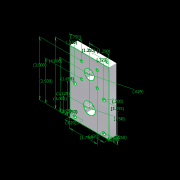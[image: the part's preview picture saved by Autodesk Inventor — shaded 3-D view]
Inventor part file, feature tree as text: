
AUTODESK INVENTOR PART (.ipt)
format: ipt  version: 2012 (Build 160160000, 160)  size: 161,792 bytes
history: native  units: in
note: dims shown in document units (in); Inventor stores cm internally (conversion verified against a paired STEP export)
features: hole x12, other x2, sketch x2, extrude x1
ambient origin geometry x8: Origin, YZ Plane, XZ Plane, XY Plane, X Axis, Y Axis, Z Axis, Center Point
bodies: Solid1 (feature_tree)
feature tree (17):
  extrude  "Extrusion1"  Depth=4.0in
  hole  "Hole15"  [1 undecoded]
  hole  "Hole16"  [1 undecoded]
  hole  "Hole17"  [1 undecoded]
  hole  "Hole18"  [1 undecoded]
  hole  "Hole19"  [1 undecoded]
  hole  "Hole20"  [1 undecoded]
  hole  "Hole23"  [1 undecoded]
  hole  "Hole24"  [1 undecoded]
  other  "Font"
  other  "Side"
  hole  "Hole25"  [1 undecoded]
  hole  "Hole26"  [1 undecoded]
  hole  "Hole27"  [1 undecoded]
  hole  "Hole28"  [1 undecoded]
  sketch  "Sketch5"  dims[d2=0.5in d3=0.0in d130=0.32in d131=0.195in d132=0.2in d133=0.75in d134=0.375in d135=0.25in d136=0.5635in d137=0.5in d138=0.8108in d139=0.32in d140=0.195in d141=0.2in d142=0.75in d143=0.375in d144=0.25in d145=0.5635in d146=0.5in d147=0.8108in d148=0.32in d149=2.055in d150=0.2in d151=0.75in d152=0.375in d153=0.25in d154=0.5635in d155=0.5in d156=0.8108in d157=0.32in d158=2.055in d159=0.2in d160=0.75in d161=0.375in d162=0.25in d163=0.5635in d164=0.5in d165=0.8108in d166=1.0in d167=1.25in d168=0.629in d169=0.75in d170=0.375in d171=0.25in d172=0.5635in d173=0.5in d174=0.8108in d175=1.25in d176=1.125in d177=0.75in d178=0.75in d179=0.375in d180=0.25in d181=0.5635in d182=0.5in d183=0.8108in d202=0.25in d203=0.62in d204=0.159in d205=0.75in d206=0.375in d207=0.25in d208=0.5635in d209=2.0in d210=0.8108in d211=0.25in d212=0.62in d213=0.159in d214=0.75in d215=0.375in d216=0.25in d217=0.5635in d218=2.0in d219=0.8108in d220=4.0in d221=0.2in d222=0.629in d223=0.75in d224=0.32in d225=0.195in d226=1.125in d227=3.0in d228=0.32in d229=0.195in d230=2.055in d231=2.055in d232=0.62in d233=0.5in d234=0.62in d235=0.25in d236=0.25in d237=1.25in d238=1.25in d239=0.75in d240=3.5in d241=0.155in d242=0.75in d243=0.375in d244=0.25in d245=0.5635in d246=1.0in d247=0.8108in d248=0.75in d249=2.5in d250=0.155in d251=0.75in d252=0.375in d253=0.25in d254=0.5635in d255=1.0in d256=0.8108in d257=1.75in d258=3.5in d259=0.155in d260=0.75in d261=0.375in d262=0.25in d263=0.5635in d264=1.0in d265=0.8108in d266=1.75in d267=2.5in d268=0.155in d269=0.75in d270=0.375in d271=0.25in d272=0.5635in d273=1.0in d274=0.8108in d275=2.5in d276=0.75in d277=1.75in d278=3.5in d13=1.0in d14=1.0in d40=1.0in d41=1.0in]
  sketch  "Sketch1"  dims[d0=2.5in d1=4.0in]
note: 12 required parameter values undecoded (feature->parameter linkage not recoverable at this tier; creation-order binding heuristic only, values carry confidence <= 0.55)
